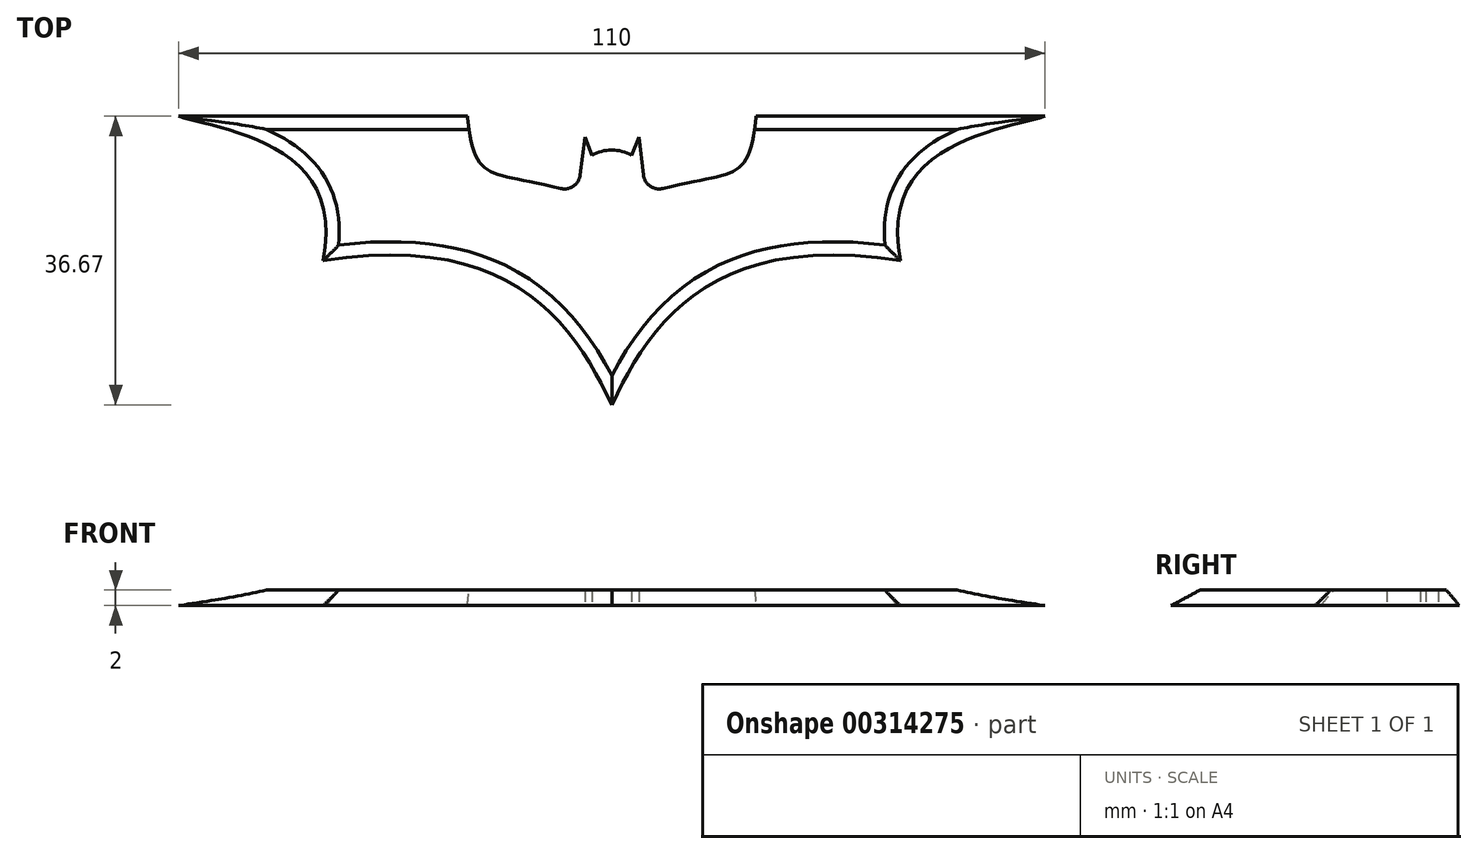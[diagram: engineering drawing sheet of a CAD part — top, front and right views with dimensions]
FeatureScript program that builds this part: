
annotation { "Feature Type Name" : "Feature", "Feature Type Description" : "" }
export const myFeature = defineFeature(function(context is Context, id is Id, definition is map)
    precondition{}
    {
        {
            assignVariable(context, id + "F0", {"name" : "thickness", "anyValue" : 2});
        }
        {
            var Q0;
            Q0=qCreatedBy(makeId("Top.planeOp"),FACE);
            var sketch = newSketch(context, id + "F1", { "sketchPlane" : qUnion([Q0])});
            skLineSegment(sketch, "E0", {"start": v(-55, 0) * mm, "end": v(-18.33, 0) * mm});
            skFitSpline(sketch, "E1", {"points": [v(-55, 0) * mm, v(-36.67, -18.33) * mm], "startDerivative": vector(19.44, -5.95) * mm, "endDerivative": vector(-8.73, -44.33) * mm});
            skFitSpline(sketch, "E2", {"points": [v(-36.67, -18.33) * mm, v(0, -36.67) * mm], "startDerivative": vector(73.1, 11.4) * mm, "endDerivative": vector(14.25, -29.82) * mm});
            skLineSegment(sketch, "E3", {"start": v(-3.43, -2.66) * mm, "end": v(-4.02, -7.48) * mm});
            skFitSpline(sketch, "E4", {"points": [v(-18.33, 0) * mm, v(-4.3, -9.77) * mm], "startDerivative": vector(2.79, -27.6) * mm, "endDerivative": vector(33.49, -9.74) * mm});
            skLineSegment(sketch, "E5", {"start": v(-3.43, -2.66) * mm, "end": v(-2.53, -4.98) * mm});
            skLineSegment(sketch, "E6.MirrorCS", {"start": v(3.43, -2.66) * mm, "end": v(4.02, -7.48) * mm});
            skFitSpline(sketch, "E7.MirrorCS", {"points": [v(18.33, 0) * mm, v(4.3, -9.77) * mm], "startDerivative": vector(-2.79, -27.6) * mm, "endDerivative": vector(-33.49, -9.74) * mm});
            skLineSegment(sketch, "E8.MirrorCS", {"start": v(3.43, -2.66) * mm, "end": v(2.53, -4.98) * mm});
            skLineSegment(sketch, "E9.MirrorCS", {"start": v(55, 0) * mm, "end": v(18.33, 0) * mm});
            skFitSpline(sketch, "E10.MirrorCS", {"points": [v(55, 0) * mm, v(36.67, -18.33) * mm], "startDerivative": vector(-19.44, -5.95) * mm, "endDerivative": vector(8.73, -44.33) * mm});
            skFitSpline(sketch, "E11.MirrorCS", {"points": [v(36.67, -18.33) * mm, v(0, -36.67) * mm], "startDerivative": vector(-73.1, 11.4) * mm, "endDerivative": vector(-14.25, -29.82) * mm});
            skArc(sketch, "E12", {"start": v(2.53, -4.98) * mm, "mid": v(0, -4.3) * mm, "end": v(-2.53, -4.98) * mm});
            skLineSegment(sketch, "E13", {"start": v(-36.67, -18.33) * mm, "end": v(-34.94, -9.55) * mm, "construction": true});
            skLineSegment(sketch, "E14", {"start": v(-36.67, -18.33) * mm, "end": v(-31.82, -17.58) * mm, "construction": true});
            skArc(sketch, "E15.filletArc", {"start": v(-6.5, -9.17) * mm, "mid": v(-4.88, -8.89) * mm, "end": v(-4.02, -7.48) * mm});
            skArc(sketch, "E16.filletArc", {"start": v(4.02, -7.48) * mm, "mid": v(4.88, -8.89) * mm, "end": v(6.5, -9.17) * mm});
            skLineSegment(sketch, "E17.bottom", {"start": v(-18.33, 0) * mm, "end": v(-36.67, 0) * mm, "construction": true});
            skLineSegment(sketch, "E17.top", {"start": v(-18.33, -18.33) * mm, "end": v(-36.67, -18.33) * mm, "construction": true});
            skLineSegment(sketch, "E17.left", {"start": v(-18.33, 0) * mm, "end": v(-18.33, -18.33) * mm, "construction": true});
            skLineSegment(sketch, "E17.right", {"start": v(-36.67, 0) * mm, "end": v(-36.67, -18.33) * mm, "construction": true});
            skSolve(sketch);
        }
        {
            var Q0;
            Q0=makeQuery(id+"F1.imprint","IMPRINT",FACE,{"disambiguationData":[TD([[makeQuery(id+"F1.imprint","IMPRINT",EDGE,{"derivedFrom":sQuery(id+"F1.wireOp",EDGE,"E0")}),-1.0]])]});
            extrude(context, id + "F2", {"entities" : qUnion([Q0]), "depth" : getVariable(context, 'thickness') * mm});
        }
        {
            var Q0;
            Q0=makeQuery(id+"F2.opExtrude","CAP_EDGE",EDGE,{"disambiguationData":[OSD([sQuery(id+"F1.wireOp",EDGE,"E1")])],"isStart":false});
            var Q1;
            Q1=makeQuery(id+"F2.opExtrude","CAP_EDGE",EDGE,{"disambiguationData":[OSD([sQuery(id+"F1.wireOp",EDGE,"E0")])],"isStart":false});
            var Q2;
            Q2=makeQuery(id+"F2.opExtrude","CAP_EDGE",EDGE,{"disambiguationData":[OSD([sQuery(id+"F1.wireOp",EDGE,"E2")])],"isStart":false});
            var Q3;
            Q3=makeQuery(id+"F2.opExtrude","CAP_EDGE",EDGE,{"disambiguationData":[OSD([sQuery(id+"F1.wireOp",EDGE,"E11.MirrorCS")])],"isStart":false});
            var Q4;
            Q4=makeQuery(id+"F2.opExtrude","CAP_EDGE",EDGE,{"disambiguationData":[OSD([sQuery(id+"F1.wireOp",EDGE,"E10.MirrorCS")])],"isStart":false});
            var Q5;
            Q5=makeQuery(id+"F2.opExtrude","CAP_EDGE",EDGE,{"disambiguationData":[OSD([sQuery(id+"F1.wireOp",EDGE,"E9.MirrorCS")])],"isStart":false});
            chamfer(context, id + "F3", {"entities" : qUnion([Q0, Q1, Q2, Q3, Q4, Q5]), "chamferType" : ChamferType.OFFSET_ANGLE, "width" : (getVariable(context, 'thickness')) * mm, "oppositeDirection" : true, "angle" : 40 * degree, "tangentPropagation" : true});
        }
    });
